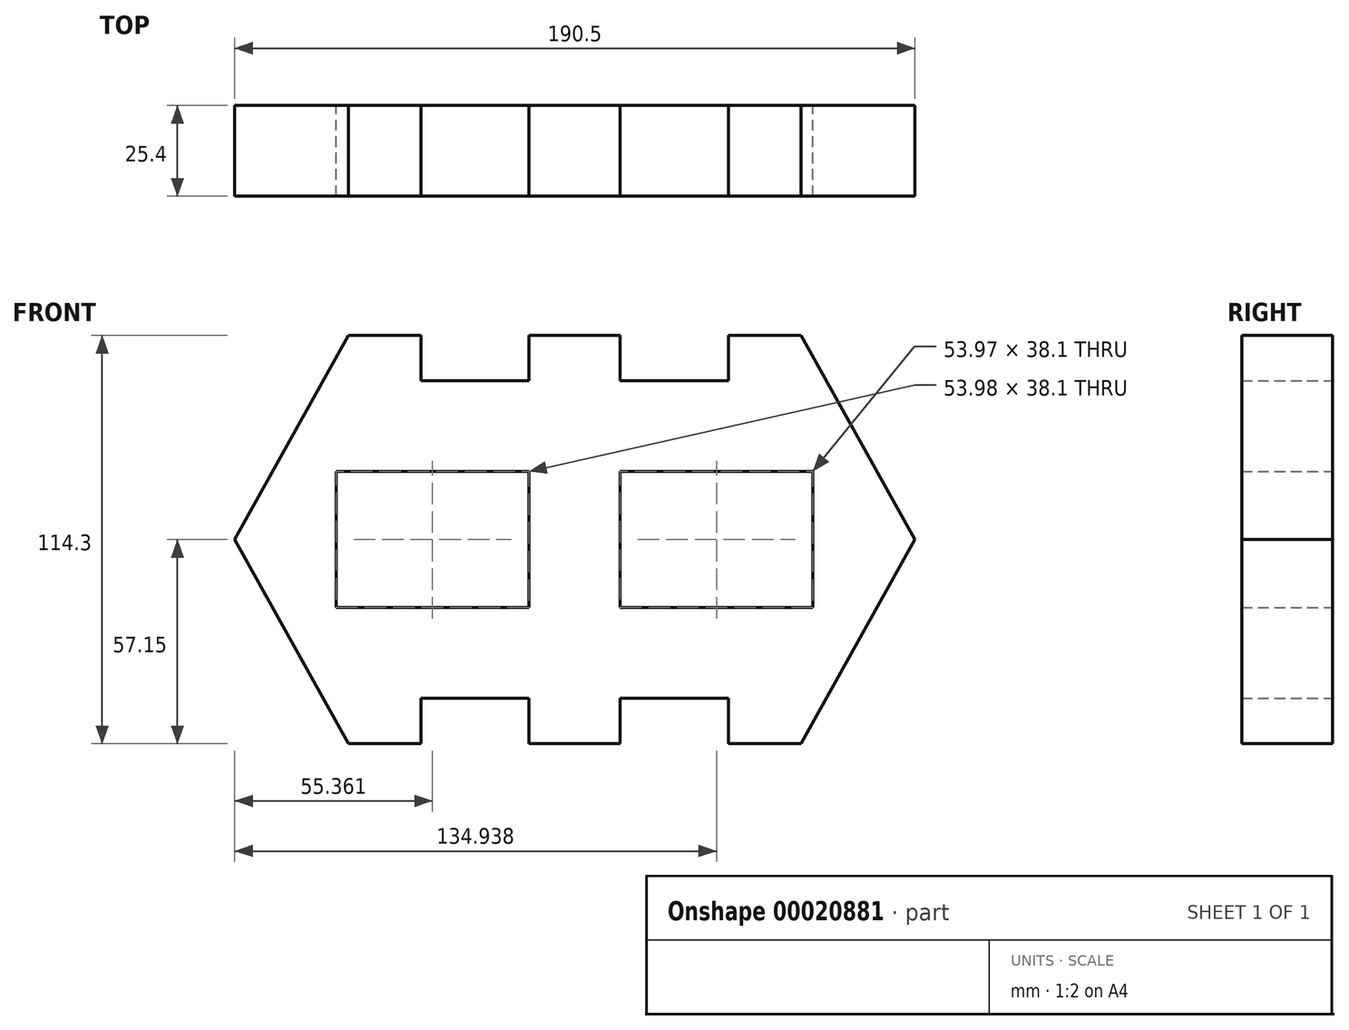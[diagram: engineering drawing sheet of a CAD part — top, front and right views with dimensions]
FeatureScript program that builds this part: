
annotation { "Feature Type Name" : "Feature", "Feature Type Description" : "" }
export const myFeature = defineFeature(function(context is Context, id is Id, definition is map)
    precondition{}
    {
        {
            var Q0;
            Q0=qCreatedBy(makeId("Front.planeOp"),FACE);
            var sketch = newSketch(context, id + "F0", { "sketchPlane" : qUnion([Q0])});
            skLineSegment(sketch, "E0.rect.bottom", {"start": v(63.4, -57.15) * mm, "end": v(43.06, -57.15) * mm});
            skLineSegment(sketch, "E0.rect.top", {"start": v(63.4, 57.15) * mm, "end": v(43.06, 57.15) * mm});
            skPoint(sketch, "E0.rect.middle", {"position": v(0, 0) * mm});
            skLineSegment(sketch, "E1", {"start": v(-63.4, 57.15) * mm, "end": v(-95.25, 0) * mm});
            skLineSegment(sketch, "E2", {"start": v(-95.25, 0) * mm, "end": v(-63.4, -57.15) * mm});
            skLineSegment(sketch, "E3", {"start": v(-43.06, 57.15) * mm, "end": v(-63.4, 57.15) * mm});
            skLineSegment(sketch, "E4", {"start": v(-43.06, -57.15) * mm, "end": v(-63.4, -57.15) * mm});
            skLineSegment(sketch, "E5.MirrorCS", {"start": v(63.4, 57.15) * mm, "end": v(95.25, 0) * mm});
            skLineSegment(sketch, "E6.MirrorCS", {"start": v(43.06, -57.15) * mm, "end": v(63.4, -57.15) * mm});
            skLineSegment(sketch, "E7.MirrorCS", {"start": v(95.25, 0) * mm, "end": v(63.4, -57.15) * mm});
            skLineSegment(sketch, "E8.MirrorCS", {"start": v(43.06, 57.15) * mm, "end": v(63.4, 57.15) * mm});
            skLineSegment(sketch, "E9", {"start": v(-12.9, -44.45) * mm, "end": v(-43.06, -44.45) * mm});
            skLineSegment(sketch, "E10", {"start": v(43.06, -44.45) * mm, "end": v(12.7, -44.45) * mm});
            skLineSegment(sketch, "E11", {"start": v(-12.9, 44.45) * mm, "end": v(-43.06, 44.45) * mm});
            skLineSegment(sketch, "E12", {"start": v(12.7, 44.45) * mm, "end": v(43.06, 44.45) * mm});
            skPoint(sketch, "E13.orphan", {"position": v(0, -44.45) * mm});
            skLineSegment(sketch, "E14.trimOffspring", {"start": v(12.7, -57.15) * mm, "end": v(-12.9, -57.15) * mm});
            skLineSegment(sketch, "E15.trimOffspring", {"start": v(12.7, 57.15) * mm, "end": v(-12.9, 57.15) * mm});
            skPoint(sketch, "E16.end.orphan", {"position": v(-95.25, 57.15) * mm});
            skLineSegment(sketch, "E17", {"start": v(-43.06, 44.45) * mm, "end": v(-43.06, 57.15) * mm});
            skLineSegment(sketch, "E18", {"start": v(-43.06, -44.45) * mm, "end": v(-43.06, -57.15) * mm});
            skLineSegment(sketch, "E19", {"start": v(-12.9, 57.15) * mm, "end": v(-12.9, 44.45) * mm});
            skLineSegment(sketch, "E20", {"start": v(-12.9, -44.45) * mm, "end": v(-12.9, -57.15) * mm});
            skLineSegment(sketch, "E21", {"start": v(12.7, 57.15) * mm, "end": v(12.7, 44.45) * mm});
            skLineSegment(sketch, "E22", {"start": v(12.7, -44.45) * mm, "end": v(12.7, -57.15) * mm});
            skLineSegment(sketch, "E23", {"start": v(43.06, 57.15) * mm, "end": v(43.06, 44.45) * mm});
            skLineSegment(sketch, "E24", {"start": v(43.06, -44.45) * mm, "end": v(43.06, -57.15) * mm});
            skLineSegment(sketch, "E25", {"start": v(-12.9, 19.05) * mm, "end": v(-66.88, 19.05) * mm});
            skLineSegment(sketch, "E26", {"start": v(12.7, 19.05) * mm, "end": v(66.68, 19.05) * mm});
            skLineSegment(sketch, "E27", {"start": v(-12.9, -19.05) * mm, "end": v(-66.88, -19.05) * mm});
            skLineSegment(sketch, "E28", {"start": v(12.7, -19.05) * mm, "end": v(66.68, -19.05) * mm});
            skLineSegment(sketch, "E29", {"start": v(-66.88, 19.05) * mm, "end": v(-66.88, -19.05) * mm});
            skLineSegment(sketch, "E30", {"start": v(66.68, 19.05) * mm, "end": v(66.68, -19.05) * mm});
            skLineSegment(sketch, "E31", {"start": v(-12.9, 19.05) * mm, "end": v(-12.9, -19.05) * mm});
            skLineSegment(sketch, "E32", {"start": v(12.7, 19.05) * mm, "end": v(12.7, -19.05) * mm});
            skSolve(sketch);
        }
        {
            var Q0;
            Q0 = qSketchRegion(id + "F0", true);
            extrude(context, id + "F1", {"entities" : qUnion([Q0]), "depth" : 25.4 * mm});
        }
    });
